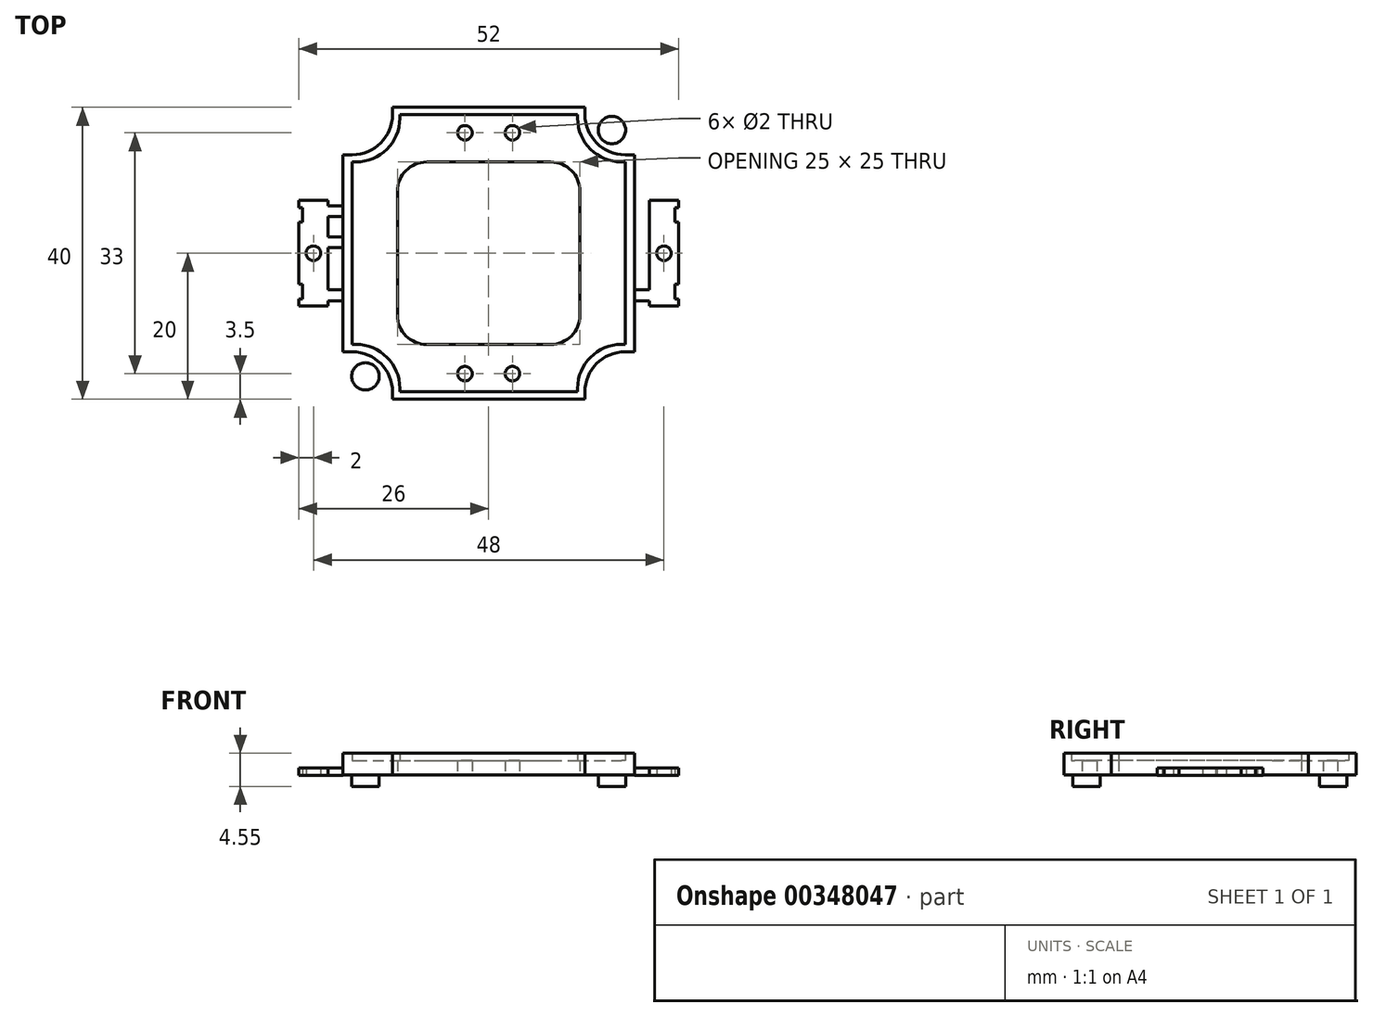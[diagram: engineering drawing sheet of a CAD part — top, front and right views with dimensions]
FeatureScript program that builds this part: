
annotation { "Feature Type Name" : "Feature", "Feature Type Description" : "" }
export const myFeature = defineFeature(function(context is Context, id is Id, definition is map)
    precondition{}
    {
        {
            var Q0;
            Q0=qCreatedBy(makeId("Top.planeOp"),FACE);
            var sketch = newSketch(context, id + "F0", { "sketchPlane" : qUnion([Q0])});
            skLineSegment(sketch, "E0.bottom", {"start": v(-20, 21) * mm, "end": v(20, 21) * mm});
            skLineSegment(sketch, "E0.top", {"start": v(-20, -21) * mm, "end": v(20, -21) * mm});
            skLineSegment(sketch, "E0.left", {"start": v(-20, 21) * mm, "end": v(-20, -21) * mm});
            skLineSegment(sketch, "E0.right", {"start": v(20, 21) * mm, "end": v(20, -21) * mm});
            skPoint(sketch, "E0.middle", {"position": v(0, 0) * mm});
            skLineSegment(sketch, "E1.bottom", {"start": v(-20, 5) * mm, "end": v(-22, 5) * mm});
            skLineSegment(sketch, "E1.top", {"start": v(-20, 6.5) * mm, "end": v(-22, 6.5) * mm});
            skLineSegment(sketch, "E1.left", {"start": v(-20, 6.5) * mm, "end": v(-20, 5) * mm});
            skLineSegment(sketch, "E2.bottom", {"start": v(-20, 0.75) * mm, "end": v(-22, 0.75) * mm});
            skLineSegment(sketch, "E2.top", {"start": v(-20, 2.25) * mm, "end": v(-22, 2.25) * mm});
            skLineSegment(sketch, "E2.left", {"start": v(-20, 2.25) * mm, "end": v(-20, 0.75) * mm});
            skLineSegment(sketch, "E3.MirrorCS", {"start": v(-20, -6.5) * mm, "end": v(-22, -6.5) * mm});
            skLineSegment(sketch, "E4.MirrorCS", {"start": v(-20, -5) * mm, "end": v(-22, -5) * mm});
            skLineSegment(sketch, "E5.bottom", {"start": v(-26, 7.25) * mm, "end": v(-22, 7.25) * mm});
            skLineSegment(sketch, "E5.top", {"start": v(-26, -7.25) * mm, "end": v(-22, -7.25) * mm});
            skLineSegment(sketch, "E5.left", {"start": v(-26, 7.25) * mm, "end": v(-26, 6.25) * mm});
            skLineSegment(sketch, "E5.right", {"start": v(-22, 7.25) * mm, "end": v(-22, 5) * mm});
            skCircle(sketch, "E6", {"center": v(-24, 0) * mm, "radius": 1 * mm});
            skLineSegment(sketch, "E7.MirrorCS", {"start": v(22, 2.25) * mm, "end": v(22, 0.75) * mm});
            skLineSegment(sketch, "E8.MirrorCS", {"start": v(20, 2.25) * mm, "end": v(20, 0.75) * mm});
            skLineSegment(sketch, "E9.MirrorCS", {"start": v(20, 6.5) * mm, "end": v(20, 5) * mm});
            skLineSegment(sketch, "E10.MirrorCS", {"start": v(22, 7.25) * mm, "end": v(22, 5) * mm});
            skLineSegment(sketch, "E11.MirrorCS", {"start": v(26, 7.25) * mm, "end": v(26, 6.25) * mm});
            skCircle(sketch, "E12.MirrorC", {"center": v(24, 0) * mm, "radius": 1 * mm});
            skLineSegment(sketch, "E13.MirrorCS", {"start": v(20, 2.25) * mm, "end": v(22, 2.25) * mm});
            skLineSegment(sketch, "E14.MirrorCS", {"start": v(26, -7.25) * mm, "end": v(22, -7.25) * mm});
            skLineSegment(sketch, "E15.MirrorCS", {"start": v(20, -6.5) * mm, "end": v(22, -6.5) * mm});
            skLineSegment(sketch, "E16.MirrorCS", {"start": v(20, 0.75) * mm, "end": v(22, 0.75) * mm});
            skLineSegment(sketch, "E17.MirrorCS", {"start": v(20, 5) * mm, "end": v(22, 5) * mm});
            skLineSegment(sketch, "E18.MirrorCS", {"start": v(20, -5) * mm, "end": v(22, -5) * mm});
            skLineSegment(sketch, "E19.MirrorCS", {"start": v(20, 6.5) * mm, "end": v(22, 6.5) * mm});
            skLineSegment(sketch, "E20.MirrorCS", {"start": v(26, 7.25) * mm, "end": v(22, 7.25) * mm});
            skLineSegment(sketch, "E21.trimOffspring", {"start": v(-22, 6.5) * mm, "end": v(-22, -6.5) * mm});
            skLineSegment(sketch, "E22.trimOffspring", {"start": v(-22, -5) * mm, "end": v(-22, -7.25) * mm});
            skPoint(sketch, "E23.MirrorCS.start.orphan", {"position": v(-22, -5) * mm});
            skLineSegment(sketch, "E24.trimOffspring", {"start": v(22, 6.5) * mm, "end": v(22, -6.5) * mm});
            skPoint(sketch, "E25.MirrorCS.end.orphan", {"position": v(22, -6.5) * mm});
            skPoint(sketch, "E25.MirrorCS.start.orphan", {"position": v(22, -5) * mm});
            skLineSegment(sketch, "E26.trimOffspring", {"start": v(22, -5) * mm, "end": v(22, -7.25) * mm});
            skLineSegment(sketch, "E27.bottom", {"start": v(-26, 6.25) * mm, "end": v(-25.5, 6.25) * mm});
            skLineSegment(sketch, "E27.top", {"start": v(-26, 4.25) * mm, "end": v(-25.5, 4.25) * mm});
            skLineSegment(sketch, "E27.right", {"start": v(-25.5, 6.25) * mm, "end": v(-25.5, 4.25) * mm});
            skLineSegment(sketch, "E28.MirrorCS", {"start": v(-26, -4.25) * mm, "end": v(-25.5, -4.25) * mm});
            skLineSegment(sketch, "E29.MirrorCS", {"start": v(-25.5, -6.25) * mm, "end": v(-25.5, -4.25) * mm});
            skLineSegment(sketch, "E30.MirrorCS", {"start": v(-26, -6.25) * mm, "end": v(-25.5, -6.25) * mm});
            skLineSegment(sketch, "E31.MirrorCS", {"start": v(25.5, 6.25) * mm, "end": v(25.5, 4.25) * mm});
            skLineSegment(sketch, "E32.MirrorCS", {"start": v(26, 6.25) * mm, "end": v(25.5, 6.25) * mm});
            skLineSegment(sketch, "E33.MirrorCS", {"start": v(26, 4.25) * mm, "end": v(25.5, 4.25) * mm});
            skLineSegment(sketch, "E34.MirrorCS", {"start": v(25.5, -6.25) * mm, "end": v(25.5, -4.25) * mm});
            skLineSegment(sketch, "E35.MirrorCS", {"start": v(26, -4.25) * mm, "end": v(25.5, -4.25) * mm});
            skLineSegment(sketch, "E36.MirrorCS", {"start": v(26, -6.25) * mm, "end": v(25.5, -6.25) * mm});
            skLineSegment(sketch, "E37.trimOffspring", {"start": v(-26, 4.25) * mm, "end": v(-26, -4.25) * mm});
            skLineSegment(sketch, "E38.trimOffspring", {"start": v(-26, -6.25) * mm, "end": v(-26, -7.25) * mm});
            skLineSegment(sketch, "E39.trimOffspring", {"start": v(26, 4.25) * mm, "end": v(26, -4.25) * mm});
            skLineSegment(sketch, "E40.trimOffspring", {"start": v(26, -6.25) * mm, "end": v(26, -7.25) * mm});
            skSolve(sketch);
        }
        {
            var Q0;
            Q0=makeQuery(id+"F0.imprint","IMPRINT",FACE,{"disambiguationData":[TD([[makeQuery(id+"F0.imprint","IMPRINT",EDGE,{"derivedFrom":sQuery(id+"F0.wireOp",EDGE,"E0.bottom")}),-1.0]])]});
            extrude(context, id + "F1", {"entities" : qUnion([Q0]), "depth" : 1.55 * mm});
        }
        {
            var Q0;
            Q0=makeQuery(id+"F1.opExtrude","CAP_FACE",FACE,{"disambiguationData":[OSD([sQuery(id+"F0.wireOp",EDGE,"E0.bottom"),sQuery(id+"F0.wireOp",EDGE,"E0.top"),sQuery(id+"F0.wireOp",EDGE,"E0.left"),sQuery(id+"F0.wireOp",EDGE,"E0.right")])],"isStart":false});
            var sketch = newSketch(context, id + "F2", { "sketchPlane" : qUnion([Q0])});
            skLineSegment(sketch, "E41.bottom", {"start": v(-13.17, 20) * mm, "end": v(13.17, 20) * mm});
            skLineSegment(sketch, "E41.top", {"start": v(-13.17, -20) * mm, "end": v(13.17, -20) * mm});
            skLineSegment(sketch, "E41.left", {"start": v(-20, 13.5) * mm, "end": v(-20, -13.5) * mm});
            skLineSegment(sketch, "E41.right", {"start": v(20, 13.5) * mm, "end": v(20, -13.5) * mm});
            skPoint(sketch, "E41.middle", {"position": v(0, 0) * mm});
            skLineSegment(sketch, "E42.top", {"start": v(20, 13.5) * mm, "end": v(18.67, 13.5) * mm});
            skLineSegment(sketch, "E42.right", {"start": v(13.17, 20) * mm, "end": v(13.17, 19) * mm});
            skPoint(sketch, "E43.visualSharp", {"position": v(13.17, 13.5) * mm});
            skArc(sketch, "E43.filletArc", {"start": v(13.17, 19) * mm, "mid": v(14.78, 15.11) * mm, "end": v(18.67, 13.5) * mm});
            skLineSegment(sketch, "E44.MirrorCS", {"start": v(-13.17, 20) * mm, "end": v(-13.17, 19) * mm});
            skArc(sketch, "E45.MirrorCS", {"start": v(-13.17, 19) * mm, "mid": v(-14.78, 15.11) * mm, "end": v(-18.67, 13.5) * mm});
            skLineSegment(sketch, "E46.MirrorCS", {"start": v(-20, 13.5) * mm, "end": v(-18.67, 13.5) * mm});
            skArc(sketch, "E47.MirrorCS", {"start": v(-13.17, -19) * mm, "mid": v(-14.78, -15.11) * mm, "end": v(-18.67, -13.5) * mm});
            skLineSegment(sketch, "E48.MirrorCS", {"start": v(-20, -13.5) * mm, "end": v(-18.67, -13.5) * mm});
            skLineSegment(sketch, "E49.MirrorCS", {"start": v(-13.17, -20) * mm, "end": v(-13.17, -19) * mm});
            skLineSegment(sketch, "E50.MirrorCS", {"start": v(20, -13.5) * mm, "end": v(18.67, -13.5) * mm});
            skArc(sketch, "E51.MirrorCS", {"start": v(13.17, -19) * mm, "mid": v(14.78, -15.11) * mm, "end": v(18.67, -13.5) * mm});
            skLineSegment(sketch, "E52.MirrorCS", {"start": v(13.17, -20) * mm, "end": v(13.17, -19) * mm});
            skPoint(sketch, "E53.orphan", {"position": v(-20, 20) * mm});
            skLineSegment(sketch, "E54.bottom", {"start": v(-12.17, 19) * mm, "end": v(12.17, 19) * mm});
            skLineSegment(sketch, "E54.top", {"start": v(-12.17, -19) * mm, "end": v(12.17, -19) * mm});
            skLineSegment(sketch, "E54.left", {"start": v(-18.67, 12.5) * mm, "end": v(-18.67, -12.5) * mm});
            skLineSegment(sketch, "E55.top", {"start": v(-18.67, 12.5) * mm, "end": v(-18.17, 12.5) * mm});
            skLineSegment(sketch, "E55.right", {"start": v(-12.17, 19) * mm, "end": v(-12.17, 18.5) * mm});
            skPoint(sketch, "E56.visualSharp", {"position": v(-12.17, 12.5) * mm});
            skArc(sketch, "E56.filletArc", {"start": v(-18.17, 12.5) * mm, "mid": v(-13.93, 14.26) * mm, "end": v(-12.17, 18.5) * mm});
            skArc(sketch, "E57.MirrorCS", {"start": v(18.17, 12.5) * mm, "mid": v(13.93, 14.26) * mm, "end": v(12.17, 18.5) * mm});
            skLineSegment(sketch, "E58.MirrorCS", {"start": v(12.17, 19) * mm, "end": v(12.17, 18.5) * mm});
            skLineSegment(sketch, "E59.MirrorCS", {"start": v(18.67, 12.5) * mm, "end": v(18.17, 12.5) * mm});
            skArc(sketch, "E60.MirrorCS", {"start": v(18.17, -12.5) * mm, "mid": v(13.93, -14.26) * mm, "end": v(12.17, -18.5) * mm});
            skArc(sketch, "E61.MirrorCS", {"start": v(-18.17, -12.5) * mm, "mid": v(-13.93, -14.26) * mm, "end": v(-12.17, -18.5) * mm});
            skLineSegment(sketch, "E62.MirrorCS", {"start": v(-12.17, -19) * mm, "end": v(-12.17, -18.5) * mm});
            skLineSegment(sketch, "E63.MirrorCS", {"start": v(-18.67, -12.5) * mm, "end": v(-18.17, -12.5) * mm});
            skLineSegment(sketch, "E64.MirrorCS", {"start": v(18.67, -12.5) * mm, "end": v(18.17, -12.5) * mm});
            skLineSegment(sketch, "E65.MirrorCS", {"start": v(12.17, -19) * mm, "end": v(12.17, -18.5) * mm});
            skLineSegment(sketch, "E66.trimOffspring", {"start": v(18.67, 12.5) * mm, "end": v(18.67, -12.5) * mm});
            skPoint(sketch, "E54.right.start.orphan", {"position": v(19, 19) * mm});
            skLineSegment(sketch, "E67.bottom", {"start": v(-9.17, -18) * mm, "end": v(-9.67, -18) * mm});
            skLineSegment(sketch, "E67.top", {"start": v(-9.17, -14.5) * mm, "end": v(-9.67, -14.5) * mm});
            skLineSegment(sketch, "E67.left", {"start": v(-9.17, -18) * mm, "end": v(-9.17, -14.5) * mm});
            skLineSegment(sketch, "E67.right", {"start": v(-9.67, -18) * mm, "end": v(-9.67, -14.5) * mm});
            skLineSegment(sketch, "E68.bottom", {"start": v(-11.17, -15.98) * mm, "end": v(-7.67, -15.98) * mm});
            skLineSegment(sketch, "E68.top", {"start": v(-11.17, -16.48) * mm, "end": v(-7.67, -16.48) * mm});
            skLineSegment(sketch, "E68.left", {"start": v(-11.17, -15.98) * mm, "end": v(-11.17, -16.48) * mm});
            skLineSegment(sketch, "E68.right", {"start": v(-7.67, -15.98) * mm, "end": v(-7.67, -16.48) * mm});
            skPoint(sketch, "E68.middle", {"position": v(-9.42, -16.23) * mm});
            skLineSegment(sketch, "E69.bottom", {"start": v(-8.5, 12.5) * mm, "end": v(8.5, 12.5) * mm});
            skLineSegment(sketch, "E69.top", {"start": v(-8.5, -12.5) * mm, "end": v(8.5, -12.5) * mm});
            skLineSegment(sketch, "E69.left", {"start": v(-12.5, 8.5) * mm, "end": v(-12.5, -8.5) * mm});
            skLineSegment(sketch, "E69.right", {"start": v(12.5, 8.5) * mm, "end": v(12.5, -8.5) * mm});
            skPoint(sketch, "E70.visualSharp", {"position": v(-12.5, 12.5) * mm});
            skArc(sketch, "E70.filletArc", {"start": v(-8.5, 12.5) * mm, "mid": v(-11.33, 11.33) * mm, "end": v(-12.5, 8.5) * mm});
            skPoint(sketch, "E71.visualSharp", {"position": v(12.5, -12.5) * mm});
            skArc(sketch, "E71.filletArc", {"start": v(8.5, -12.5) * mm, "mid": v(11.33, -11.33) * mm, "end": v(12.5, -8.5) * mm});
            skPoint(sketch, "E72.visualSharp", {"position": v(-12.5, -12.5) * mm});
            skArc(sketch, "E72.filletArc", {"start": v(-12.5, -8.5) * mm, "mid": v(-11.33, -11.33) * mm, "end": v(-8.5, -12.5) * mm});
            skPoint(sketch, "E73.visualSharp", {"position": v(12.5, 12.5) * mm});
            skArc(sketch, "E73.filletArc", {"start": v(12.5, 8.5) * mm, "mid": v(11.33, 11.33) * mm, "end": v(8.5, 12.5) * mm});
            skCircle(sketch, "E74", {"center": v(-3.25, 16.5) * mm, "radius": 1 * mm});
            skCircle(sketch, "E75.MirrorC", {"center": v(3.25, 16.5) * mm, "radius": 1 * mm});
            skCircle(sketch, "E76.MirrorC", {"center": v(-3.25, -16.5) * mm, "radius": 1 * mm});
            skCircle(sketch, "E77.MirrorC", {"center": v(3.25, -16.5) * mm, "radius": 1 * mm});
            skSolve(sketch);
        }
        {
            var Q0;
            Q0=makeQuery(id+"F1.opExtrude","SWEPT_EDGE",EDGE,{"disambiguationData":[OSD([sQuery(id+"F0.wireOp",EDGE,"E0.bottom"),sQuery(id+"F0.wireOp",EDGE,"E0.left")])]});
            var Q1;
            Q1=makeQuery(id+"F1.opExtrude","SWEPT_EDGE",EDGE,{"disambiguationData":[OSD([sQuery(id+"F0.wireOp",EDGE,"E0.bottom"),sQuery(id+"F0.wireOp",EDGE,"E0.right")])]});
            var Q2;
            Q2=makeQuery(id+"F1.opExtrude","SWEPT_EDGE",EDGE,{"disambiguationData":[OSD([sQuery(id+"F0.wireOp",EDGE,"E0.top"),sQuery(id+"F0.wireOp",EDGE,"E0.right")])]});
            var Q3;
            Q3=makeQuery(id+"F1.opExtrude","SWEPT_EDGE",EDGE,{"disambiguationData":[OSD([sQuery(id+"F0.wireOp",EDGE,"E0.top"),sQuery(id+"F0.wireOp",EDGE,"E0.left")])]});
            chamfer(context, id + "F3", {"entities" : qUnion([Q0, Q1, Q2, Q3]), "width" : 3 * mm, "tangentPropagation" : true});
        }
        {
            var Q0;
            Q0=makeQuery(id+"F1.opExtrude","CAP_FACE",FACE,{"disambiguationData":[OSD([sQuery(id+"F0.wireOp",EDGE,"E0.bottom"),sQuery(id+"F0.wireOp",EDGE,"E0.top"),sQuery(id+"F0.wireOp",EDGE,"E0.left"),sQuery(id+"F0.wireOp",EDGE,"E0.right")])],"isStart":false});
            var sketch = newSketch(context, id + "F4", { "sketchPlane" : qUnion([Q0])});
            skCircle(sketch, "E78", {"center": v(-16.87, 16.88) * mm, "radius": 1.88 * mm});
            skCircle(sketch, "E79.MirrorC", {"center": v(16.87, 16.88) * mm, "radius": 1.88 * mm});
            skCircle(sketch, "E80.MirrorC", {"center": v(16.87, -16.88) * mm, "radius": 1.88 * mm});
            skCircle(sketch, "E81.MirrorC", {"center": v(-16.87, -16.88) * mm, "radius": 1.88 * mm});
            skSolve(sketch);
        }
        {
            var Q0;
            Q0=makeQuery(id+"F4.imprint","IMPRINT",FACE,{"disambiguationData":[TD([[makeQuery(id+"F4.imprint","IMPRINT",EDGE,{"derivedFrom":sQuery(id+"F4.wireOp",EDGE,"E81.MirrorC")}),-1.0]])]});
            var Q1;
            Q1=makeQuery(id+"F4.imprint","IMPRINT",FACE,{"disambiguationData":[TD([[makeQuery(id+"F4.imprint","IMPRINT",EDGE,{"derivedFrom":sQuery(id+"F4.wireOp",EDGE,"E80.MirrorC")}),1.0]])]});
            var Q2;
            Q2=makeQuery(id+"F4.imprint","IMPRINT",FACE,{"disambiguationData":[TD([[makeQuery(id+"F4.imprint","IMPRINT",EDGE,{"derivedFrom":sQuery(id+"F4.wireOp",EDGE,"E79.MirrorC")}),-1.0]])]});
            var Q3;
            Q3=makeQuery(id+"F4.imprint","IMPRINT",FACE,{"disambiguationData":[TD([[makeQuery(id+"F4.imprint","IMPRINT",EDGE,{"derivedFrom":sQuery(id+"F4.wireOp",EDGE,"E78")}),1.0]])]});
            extrude(context, id + "F5", {"entities" : qUnion([Q0, Q1, Q2, Q3]), "operationType" : NewBodyOperationType.REMOVE, "oppositeDirection" : true, "depth" : 4 * mm});
        }
        {
            var Q0;
            Q0=makeQuery(id+"F2.imprint","IMPRINT",FACE,{"disambiguationData":[TD([[makeQuery(id+"F2.imprint","IMPRINT",EDGE,{"derivedFrom":sQuery(id+"F2.wireOp",EDGE,"E41.bottom")}),-1.0]])]});
            extrude(context, id + "F6", {"entities" : qUnion([Q0]), "depth" : 3 * mm});
        }
        {
            var Q0;
            Q0=makeQuery(id+"F2.imprint","IMPRINT",FACE,{"disambiguationData":[TD([[makeQuery(id+"F2.imprint","IMPRINT",EDGE,{"derivedFrom":sQuery(id+"F2.wireOp",EDGE,"E54.bottom")}),-1.0]])]});
            var Q1;
            {var subQ5=sQuery(id+"F2.wireOp",EDGE,"E68.right");Q1=makeQuery(id+"F2.imprint","IMPRINT",FACE,{"disambiguationData":[TD([[makeQuery(id+"F2.imprint","IMPRINT",EDGE,{"derivedFrom":subQ5}),-1.0]])]});}
            var Q2;
            {var subQ5=sQuery(id+"F2.wireOp",EDGE,"E68.left");Q2=makeQuery(id+"F2.imprint","IMPRINT",FACE,{"disambiguationData":[TD([[makeQuery(id+"F2.imprint","IMPRINT",EDGE,{"derivedFrom":subQ5}),1.0]])]});}
            var Q3;
            {var subQ0=sQuery(id+"F2.wireOp",EDGE,"E67.bottom");Q3=makeQuery(id+"F2.imprint","IMPRINT",FACE,{"disambiguationData":[TD([[makeQuery(id+"F2.imprint","IMPRINT",EDGE,{"derivedFrom":subQ0}),-1.0]])]});}
            var Q4;
            {var subQ0=sQuery(id+"F2.wireOp",EDGE,"E67.top");Q4=makeQuery(id+"F2.imprint","IMPRINT",FACE,{"disambiguationData":[TD([[makeQuery(id+"F2.imprint","IMPRINT",EDGE,{"derivedFrom":subQ0}),1.0]])]});}
            var Q5;
            {var subQ0=sQuery(id+"F2.wireOp",EDGE,"E68.top");var subQ1=sQuery(id+"F2.wireOp",EDGE,"E67.left");var subQ2=makeQuery(id+"F2.imprint","INTERSECT",VERTEX,{"derivedFrom":[subQ1,subQ0]});Q5=makeQuery(id+"F2.imprint","IMPRINT",FACE,{"disambiguationData":[TD([[makeQuery(id+"F2.imprint","IMPRINT",EDGE,{"disambiguationData":[TD([[subQ2,-1.0]])],"derivedFrom":subQ1}),1.0]])]});}
            extrude(context, id + "F7", {"entities" : qUnion([Q0, Q1, Q2, Q3, Q4, Q5]), "operationType" : NewBodyOperationType.ADD, "depth" : 2 * mm});
        }
        {
            var Q0;
            Q0=makeQuery(id+"F2.imprint","IMPRINT",FACE,{"disambiguationData":[TD([[makeQuery(id+"F2.imprint","IMPRINT",EDGE,{"derivedFrom":sQuery(id+"F2.wireOp",EDGE,"E69.bottom")}),-1.0]])]});
            extrude(context, id + "F8", {"entities" : qUnion([Q0]), "depth" : 2 * mm});
        }
        {
            var Q0;
            Q0=makeQuery(id+"F0.imprint","IMPRINT",FACE,{"disambiguationData":[TD([[makeQuery(id+"F0.imprint","IMPRINT",EDGE,{"derivedFrom":sQuery(id+"F0.wireOp",EDGE,"E9.MirrorCS")}),1.0]])]});
            var Q1;
            Q1=makeQuery(id+"F0.imprint","IMPRINT",FACE,{"disambiguationData":[TD([[makeQuery(id+"F0.imprint","IMPRINT",EDGE,{"derivedFrom":sQuery(id+"F0.wireOp",EDGE,"E8.MirrorCS")}),1.0]])]});
            var Q2;
            {var subQ0=sQuery(id+"F0.wireOp",EDGE,"E1.bottom");Q2=makeQuery(id+"F0.imprint","IMPRINT",FACE,{"disambiguationData":[TD([[makeQuery(id+"F0.imprint","IMPRINT",EDGE,{"derivedFrom":subQ0}),-1.0]])]});}
            var Q3;
            {var subQ0=sQuery(id+"F0.wireOp",EDGE,"E2.bottom");Q3=makeQuery(id+"F0.imprint","IMPRINT",FACE,{"disambiguationData":[TD([[makeQuery(id+"F0.imprint","IMPRINT",EDGE,{"derivedFrom":subQ0}),-1.0]])]});}
            var Q4;
            {var subQ0=sQuery(id+"F0.wireOp",EDGE,"E3.MirrorCS");Q4=makeQuery(id+"F0.imprint","IMPRINT",FACE,{"disambiguationData":[TD([[makeQuery(id+"F0.imprint","IMPRINT",EDGE,{"derivedFrom":subQ0}),-1.0]])]});}
            var Q5;
            Q5=makeQuery(id+"F0.imprint","IMPRINT",FACE,{"disambiguationData":[TD([[makeQuery(id+"F0.imprint","IMPRINT",EDGE,{"derivedFrom":sQuery(id+"F0.wireOp",EDGE,"E5.bottom")}),-1.0]])]});
            var Q6;
            {var subQ0=sQuery(id+"F0.wireOp",EDGE,"E15.MirrorCS");Q6=makeQuery(id+"F0.imprint","IMPRINT",FACE,{"disambiguationData":[TD([[makeQuery(id+"F0.imprint","IMPRINT",EDGE,{"derivedFrom":subQ0}),1.0]])]});}
            var Q7;
            {var subQ6=sQuery(id+"F0.wireOp",EDGE,"E10.MirrorCS");Q7=makeQuery(id+"F0.imprint","IMPRINT",FACE,{"disambiguationData":[TD([[makeQuery(id+"F0.imprint","IMPRINT",EDGE,{"derivedFrom":subQ6}),1.0]])]});}
            extrude(context, id + "F9", {"entities" : qUnion([Q0, Q1, Q2, Q3, Q4, Q5, Q6, Q7]), "operationType" : NewBodyOperationType.ADD, "depth" : 2.5 * mm, "hasSecondDirection" : true, "secondDirectionOppositeDirection" : false, "secondDirectionDepth" : 1.5 * mm});
        }
    });
